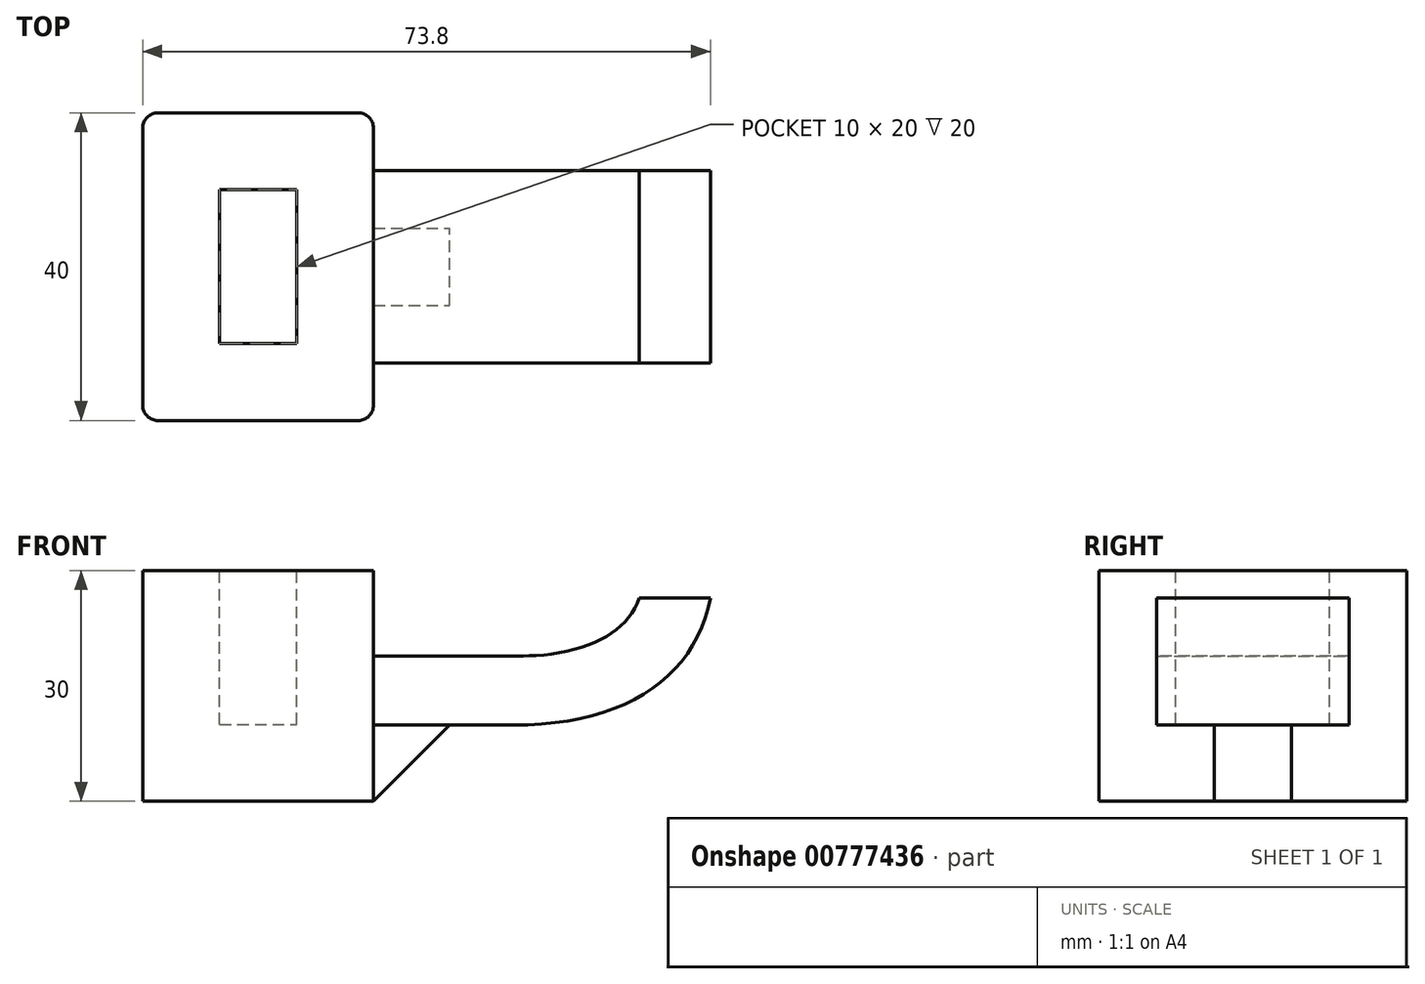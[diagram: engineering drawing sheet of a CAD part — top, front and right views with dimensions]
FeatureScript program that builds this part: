
annotation { "Feature Type Name" : "Feature", "Feature Type Description" : "" }
export const myFeature = defineFeature(function(context is Context, id is Id, definition is map)
    precondition{}
    {
        {
            var Q0;
            Q0=qCreatedBy(makeId("Front.planeOp"),FACE);
            var sketch = newSketch(context, id + "F0", { "sketchPlane" : qUnion([Q0])});
            skLineSegment(sketch, "E0.bottom", {"start": v(-128.87, 54.11) * mm, "end": v(-98.87, 54.11) * mm});
            skLineSegment(sketch, "E0.top", {"start": v(-128.87, 24.11) * mm, "end": v(-98.87, 24.11) * mm});
            skLineSegment(sketch, "E0.left", {"start": v(-128.87, 54.11) * mm, "end": v(-128.87, 24.11) * mm});
            skLineSegment(sketch, "E0.right", {"start": v(-98.87, 54.11) * mm, "end": v(-98.87, 24.11) * mm});
            skLineSegment(sketch, "E1", {"start": v(-98.87, 34.02) * mm, "end": v(-80.68, 34.02) * mm});
            skFitSpline(sketch, "E2", {"points": [v(-80.68, 34.02) * mm, v(-55.07, 50.53) * mm], "startDerivative": vector(43.65, 0) * mm, "endDerivative": vector(6.17, 31.06) * mm});
            skFitSpline(sketch, "E3.0", {"points": [v(-80.68, 43.02) * mm, v(-79.18, 43.02) * mm, v(-76.4, 43.18) * mm, v(-72.92, 43.81) * mm, v(-70.14, 44.76) * mm, v(-68.03, 45.9) * mm, v(-66.47, 47.16) * mm, v(-65.32, 48.55) * mm, v(-64.46, 50.18) * mm, v(-64.05, 51.52) * mm, v(-63.9, 52.29) * mm]});
            skLineSegment(sketch, "E3.1", {"start": v(-99.21, 43.02) * mm, "end": v(-80.68, 43.02) * mm});
            skLineSegment(sketch, "E4", {"start": v(-64.38, 50.53) * mm, "end": v(-55.07, 50.53) * mm});
            skLineSegment(sketch, "E5", {"start": v(-98.87, 24.11) * mm, "end": v(-88.97, 34.02) * mm});
            skSolve(sketch);
        }
        {
            var Q0;
            {var subQ1=sQuery(id+"F0.wireOp",EDGE,"E0.bottom");Q0=makeQuery(id+"F0.imprint","IMPRINT",FACE,{"disambiguationData":[TD([[makeQuery(id+"F0.imprint","IMPRINT",EDGE,{"derivedFrom":subQ1}),-1.0]])]});}
            extrude(context, id + "F1", {"entities" : qUnion([Q0]), "endBound" : BoundingType.SYMMETRIC, "depth" : 40 * mm, "offsetDistance" : 25 * mm});
        }
        {
            var Q0;
            {var subQ0=sQuery(id+"F0.wireOp",EDGE,"E2");Q0=makeQuery(id+"F0.imprint","IMPRINT",FACE,{"disambiguationData":[TD([[makeQuery(id+"F0.imprint","IMPRINT",EDGE,{"derivedFrom":subQ0}),1.0]])]});}
            extrude(context, id + "F2", {"entities" : qUnion([Q0]), "operationType" : NewBodyOperationType.ADD, "endBound" : BoundingType.SYMMETRIC, "depth" : 25 * mm, "offsetDistance" : 25 * mm});
        }
        {
            var Q0;
            {var subQ0=sQuery(id+"F0.wireOp",EDGE,"E5");Q0=makeQuery(id+"F0.imprint","IMPRINT",FACE,{"disambiguationData":[TD([[makeQuery(id+"F0.imprint","IMPRINT",EDGE,{"derivedFrom":subQ0}),1.0]])]});}
            extrude(context, id + "F3", {"entities" : qUnion([Q0]), "operationType" : NewBodyOperationType.ADD, "endBound" : BoundingType.SYMMETRIC, "depth" : 10 * mm, "offsetDistance" : 25 * mm});
        }
        {
            var Q0;
            Q0=makeQuery(id+"F1.opExtrude","CAP_EDGE",EDGE,{"disambiguationData":[OSD([sQuery(id+"F0.wireOp",EDGE,"E0.right")])],"isStart":false});
            var Q1;
            Q1=makeQuery(id+"F1.opExtrude","CAP_EDGE",EDGE,{"disambiguationData":[OSD([sQuery(id+"F0.wireOp",EDGE,"E0.left")])],"isStart":false});
            var Q2;
            Q2=makeQuery(id+"F1.opExtrude","CAP_EDGE",EDGE,{"disambiguationData":[OSD([sQuery(id+"F0.wireOp",EDGE,"E0.right")])],"isStart":true});
            var Q3;
            Q3=makeQuery(id+"F1.opExtrude","CAP_EDGE",EDGE,{"disambiguationData":[OSD([sQuery(id+"F0.wireOp",EDGE,"E0.left")])],"isStart":true});
            fillet(context, id + "F4", {"entities" : qUnion([Q0, Q1, Q2, Q3]), "radius" : 2 * mm, "tangentPropagation" : true, "allowEdgeOverflow" : false});
        }
        {
            var Q0;
            Q0=makeQuery(id+"F1.opExtrude","SWEPT_FACE",FACE,{"disambiguationData":[OSD([sQuery(id+"F0.wireOp",EDGE,"E0.bottom")])]});
            shell(context, id + "F5", {"entities" : qUnion([Q0]), "thickness" : 10 * mm});
        }
    });
